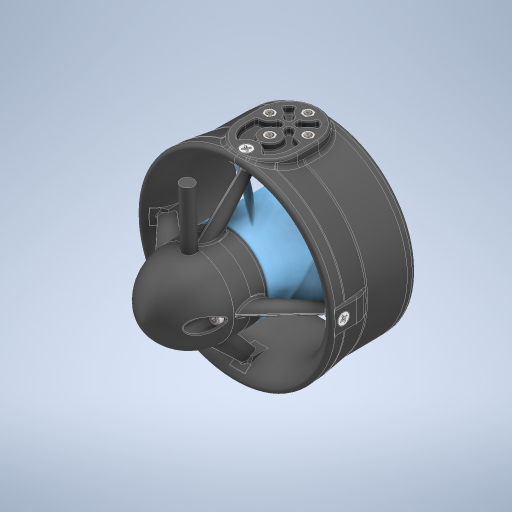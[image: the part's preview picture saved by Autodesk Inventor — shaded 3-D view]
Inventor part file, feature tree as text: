
AUTODESK INVENTOR PART (.ipt)
format: ipt  version: 2024 (Build 280153000, 153)  size: 8,168,960 bytes
history: native  units: in
note: dims shown in document units (in); Inventor stores cm internally (conversion verified against a paired STEP export)
features: other x15, extrude x1, sketch x1
ambient origin geometry x8: Origin, YZ Plane, XZ Plane, XY Plane, X Axis, Y Axis, Z Axis, Center Point
bodies: Solid1 (feature_tree), Solid2 (feature_tree), Solid3 (feature_tree), Solid4 (feature_tree), Solid5 (feature_tree), Solid6 (feature_tree), Solid7 (feature_tree), Solid8 (feature_tree), Solid9 (feature_tree), Solid10 (feature_tree), Solid11 (feature_tree), Solid12 (feature_tree), Solid13 (feature_tree), Solid14 (feature_tree)
feature tree (17):
  extrude  "Extrusion1"  Depth=1.0in TaperAngle=0.0deg
  other  "Work Point1"
  sketch  "Sketch1"  dims[d0=0.252in d1=1.0in d2=0.0in]
  other  "PUBLICT100-P-NOSE-CONE-R1-1-solid1"
  other  "PUBLICT200-P-STATOR-BASE-R1-1-solid1"
  other  "PUBLICT100-P-NOZZLE-R1-1-solid1"
  other  "PUBLICT200-P-PROPELLER-CW-XJ3-3-solid1"
  other  "PUBLICT100-F-THREADED-INSERT-R1-1-solid1"
  other  "PUBLICT100-F-THREADED-INSERT-R1-2-solid1"
  other  "PUBLICT100-F-THREADED-INSERT-R1-3-solid1"
  other  "PUBLICT100-F-THREADED-INSERT-R1-4-solid1"
  other  "PUBLICT100-F-NOZZLE-SCREW-R1-1-solid1"
  other  "PUBLICT100-F-NOZZLE-SCREW-R1-2-solid1"
  other  "PUBLICT100-F-NOZZLE-SCREW-R1-3-solid1"
  other  "PUBLICT100-F-NOZZLE-SCREW-R1-4-solid1"
  other  "PUBLICT100-F-NOSE-CONE-SCREW-R1-1-solid1"
  other  "PUBLICT100-F-NOSE-CONE-SCREW-R1-2-solid1"
